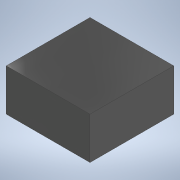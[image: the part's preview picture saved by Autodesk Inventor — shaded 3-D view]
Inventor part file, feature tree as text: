
AUTODESK INVENTOR PART (.ipt)
format: ipt  version: 2022 (Build 260153000, 153)  size: 120,832 bytes
history: native  units: mm
features: extrude x5, sketch x5
ambient origin geometry x8: Origin, YZ Plane, XZ Plane, XY Plane, X Axis, Y Axis, Z Axis, Center Point
bodies: Solid1 (feature_tree)
feature tree (10):
  extrude  "Extrusion1"  Depth=30.0mm
  extrude  "Extrusion2"  Depth=5.0mm TaperAngle=0.0deg
  extrude  "Extrusion3"  Depth=10.0mm TaperAngle=0.0deg
  extrude  "Extrusion4"  [1 undecoded]
  extrude  "Extrusion5"  [1 undecoded]
  sketch  "Sketch1"  dims[d0=30.0mm d1=30.0mm]
  sketch  "Sketch2"  dims[d2=15.0mm d3=0.0mm d4=5.0mm d5=0.0mm]
  sketch  "Sketch3"  dims[d6=10.0mm d7=0.0mm d8=10.0mm d9=0.0mm]
  sketch  "Sketch4"  dims[d10=20.0mm d11=0.0mm]
  sketch  "Sketch5"
note: 2 required parameter values undecoded (feature->parameter linkage not recoverable at this tier; creation-order binding heuristic only, values carry confidence <= 0.55)
